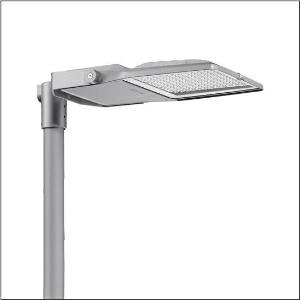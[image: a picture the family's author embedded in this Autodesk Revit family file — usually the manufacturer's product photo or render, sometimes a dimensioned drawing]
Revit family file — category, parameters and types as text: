
# Revit family: floodlight_fl_21_iq_midi___pl61_5xa7781e4c3a_96c8
name_source: partatom
category: Lighting Fixtures
units: mm (PartAtom-declared; Revit-internal decimal feet)

## family parameters
Cut with Voids When Loaded = No
Host = Face
Light Source = No
Part Type = Normal
Room Calculation Point = No
Round Connector Dimension = Use Diameter
Shared = No

## types (1)
- --- (1 x LED, 27490 lm, 208.1 W, 4000K)
    Apparent Load = 208 VA
    CIE Flux Codes = 33 65 98 100 100
    Color Rendering = 70
    Color Temperature = 4000K
    Default Elevation = 1800 mm
    Description = Floodlight FL 21 iQ midi, floodlight, primary light control with lens, of PMMA, primary optical cover: protective disc, of toughened safety glass, transparent, light distribution: PL61, light emission: direct distribution, installation type: surface-mounted, LED, High Power LED, rated luminous flux: 27.490lm, luminous efficacy: 132lm/W, light colour: 740, colour temperature: 4000K, control gear: ECG iQ, control: optimised constant luminous flux control (CLO 2.0), Desk-Remote (wireless, voltage-free reading and setting of iQ features in the workshop via application-optimized NFC function/RFID function), Light-Fading, Smart-Wire, Night-Set, Lumen-Switch, Temp-Guard, Auto-Match, with terminal, 6-pole, mains connection: 220..240V, AC, 50/60Hz, start of lifetime: 208W, end of service life: 227W, reduction: 90W, luminaire housing, of diecast aluminium, powder-coated, Siteco® metallic grey (DB 702S), corrosivity category C5 mid according to DIN EN ISO 12944, sealing non-destructively replaceable, please order mast flange separately, mast bracket, of steel, galvanised, powder-coated, Siteco® metallic grey (DB 702S), protection rating (complete): IP66, insulation class (complete): insulation class II (safety insulation), certification: CE, ENEC, VDE, protection symbol: D, impact resistance: IK08, permissible operating ambient temperature: -40..+40°C, permissible operating ambient temperature for outdoor applications: -40..+50°C, standard: DIN EN 12944, LABS conformity tested according to VDMA 24364:2018-05, packaging unit: 1 piece

Light Distribution: PL61
    Height = 76 mm
    Lamp = 1 x LED
    Lamp Light Flux = 27490 lm
    Lamp Power = 208.1 W
    Lamp count = 1
    Length = 657 mm
    Luminous efficacy = 132 lm/W
    Manufacturer = Siteco
    ModVariant = No
    Model = 5XA7781E4C3A
    Number of Poles = 1
    OnlyDefault = Yes
    Power Factor = 1
    Product Name = Floodlight FL 21 iQ midi | PL61
    Product group = floodlight | pylon annexe
    ProductGroupID = 6200
    Protection Class = Protection class II
    Protection Degree = IP 66
    RLX_Detail_Level = 1
    RLX_Emergency_Light_Flux = 0 lm
    RLX_Emergency_Type = 0
    RLX_Emergency_Type_DB = No
    RlxData = <blob elided: 153733 chars, md5=bce483a4>
    Socket = socket
    Standby Power = 0 W
    System Light Flux = 27490 lm
    System Power = 208 W
    Type Comments = factory setting: luminous flux: 100 % | dim-lin: 254 | 710 mA
    Type Image = l_1007123.jpg
    URL = http://relux.com
    VarID = @adj_077709
    Voltage = 0 V
    Weight = 0.00 kg
    Width = 442 mm

## geometry (parser evidence)
native form markers: Blend x4, Sweep x14
no freeform markers — native parametric forms only
